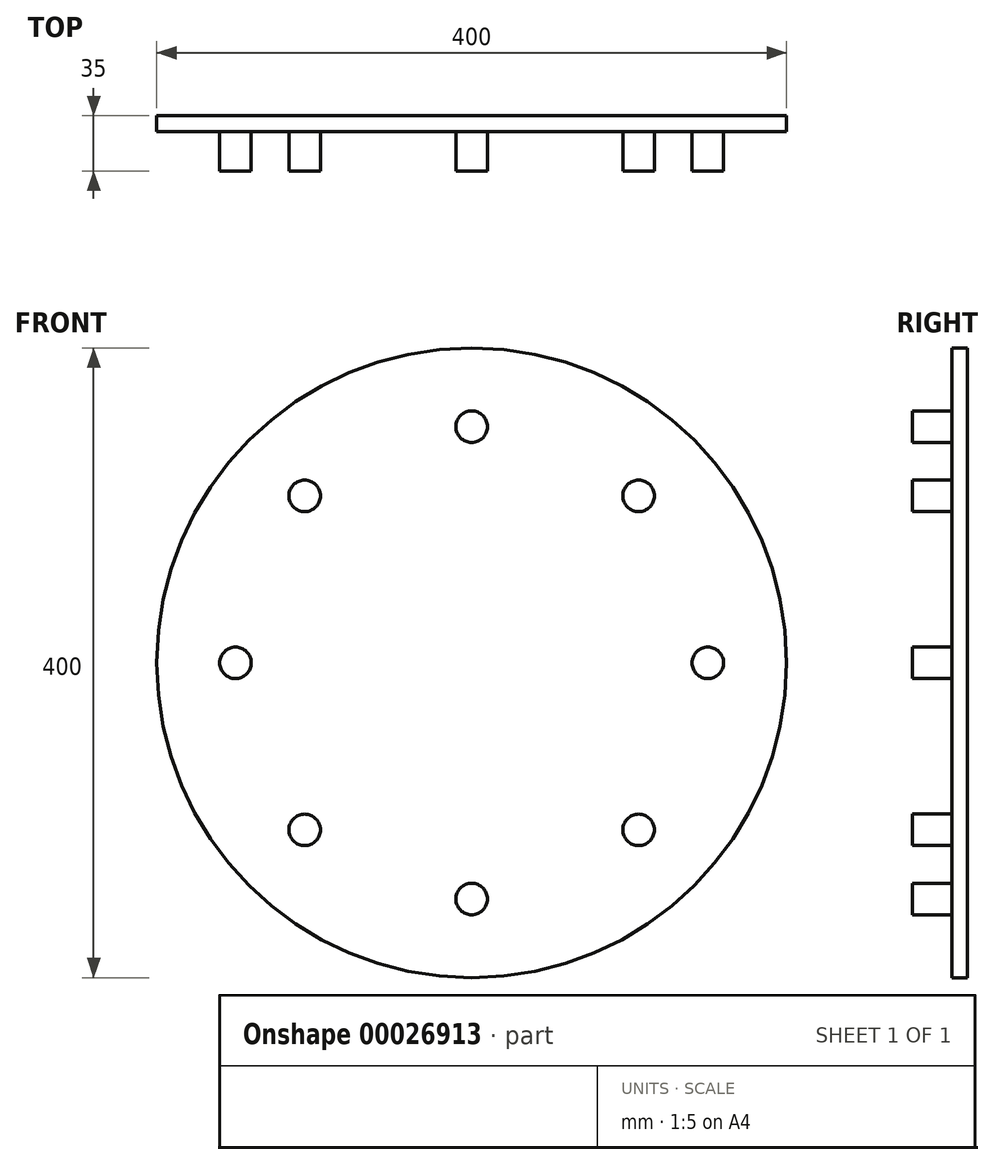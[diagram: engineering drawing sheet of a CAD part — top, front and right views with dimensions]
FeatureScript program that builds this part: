
annotation { "Feature Type Name" : "Feature", "Feature Type Description" : "" }
export const myFeature = defineFeature(function(context is Context, id is Id, definition is map)
    precondition{}
    {
        {
            var Q0;
            Q0=qCreatedBy(makeId("Front.planeOp"),FACE);
            var sketch = newSketch(context, id + "F0", { "sketchPlane" : qUnion([Q0])});
            skCircle(sketch, "E0", {"center": v(0, 0) * mm, "radius": 200 * mm});
            skSolve(sketch);
        }
        {
            var Q0;
            Q0=qSketchRegion(id+"F0",true);
            extrude(context, id + "F1", {"entities" : qUnion([Q0]), "depth" : 10 * mm});
        }
        {
            var Q0;
            Q0=makeQuery(id+"F1.opExtrude","CAP_FACE",FACE,{"disambiguationData":[OSD([sQuery(id+"F0.wireOp",EDGE,"E0")])],"isStart":false});
            var sketch = newSketch(context, id + "F2", { "sketchPlane" : qUnion([Q0])});
            skCircle(sketch, "E1", {"center": v(0, 150) * mm, "radius": 10 * mm});
            skCircle(sketch, "E2.1.0", {"center": v(-106.07, 106.07) * mm, "radius": 10 * mm});
            skCircle(sketch, "E2.2.0", {"center": v(-150, 0) * mm, "radius": 10 * mm});
            skCircle(sketch, "E2.3.0", {"center": v(-106.07, -106.07) * mm, "radius": 10 * mm});
            skCircle(sketch, "E2.4.0", {"center": v(0, -150) * mm, "radius": 10 * mm});
            skCircle(sketch, "E2.5.0", {"center": v(106.07, -106.07) * mm, "radius": 10 * mm});
            skCircle(sketch, "E2.6.0", {"center": v(150, 0) * mm, "radius": 10 * mm});
            skCircle(sketch, "E2.7.0", {"center": v(106.07, 106.07) * mm, "radius": 10 * mm});
            skPoint(sketch, "E2.center", {"position": v(0, 0) * mm});
            skSolve(sketch);
        }
        {
            var Q0;
            Q0=makeQuery(id+"F2.imprint","IMPRINT",FACE,{"disambiguationData":[TD([[makeQuery(id+"F2.imprint","IMPRINT",EDGE,{"derivedFrom":sQuery(id+"F2.wireOp",EDGE,"E2.1.0")}),1.0]])]});
            var Q1;
            Q1=makeQuery(id+"F2.imprint","IMPRINT",FACE,{"disambiguationData":[TD([[makeQuery(id+"F2.imprint","IMPRINT",EDGE,{"derivedFrom":sQuery(id+"F2.wireOp",EDGE,"E1")}),1.0]])]});
            var Q2;
            Q2=makeQuery(id+"F2.imprint","IMPRINT",FACE,{"disambiguationData":[TD([[makeQuery(id+"F2.imprint","IMPRINT",EDGE,{"derivedFrom":sQuery(id+"F2.wireOp",EDGE,"E2.7.0")}),1.0]])]});
            var Q3;
            Q3=makeQuery(id+"F2.imprint","IMPRINT",FACE,{"disambiguationData":[TD([[makeQuery(id+"F2.imprint","IMPRINT",EDGE,{"derivedFrom":sQuery(id+"F2.wireOp",EDGE,"E2.6.0")}),1.0]])]});
            var Q4;
            Q4=makeQuery(id+"F2.imprint","IMPRINT",FACE,{"disambiguationData":[TD([[makeQuery(id+"F2.imprint","IMPRINT",EDGE,{"derivedFrom":sQuery(id+"F2.wireOp",EDGE,"E2.5.0")}),1.0]])]});
            var Q5;
            Q5=makeQuery(id+"F2.imprint","IMPRINT",FACE,{"disambiguationData":[TD([[makeQuery(id+"F2.imprint","IMPRINT",EDGE,{"derivedFrom":sQuery(id+"F2.wireOp",EDGE,"E2.4.0")}),1.0]])]});
            var Q6;
            Q6=makeQuery(id+"F2.imprint","IMPRINT",FACE,{"disambiguationData":[TD([[makeQuery(id+"F2.imprint","IMPRINT",EDGE,{"derivedFrom":sQuery(id+"F2.wireOp",EDGE,"E2.3.0")}),1.0]])]});
            var Q7;
            Q7=makeQuery(id+"F2.imprint","IMPRINT",FACE,{"disambiguationData":[TD([[makeQuery(id+"F2.imprint","IMPRINT",EDGE,{"derivedFrom":sQuery(id+"F2.wireOp",EDGE,"E2.2.0")}),1.0]])]});
            extrude(context, id + "F3", {"entities" : qUnion([Q0, Q1, Q2, Q3, Q4, Q5, Q6, Q7]), "operationType" : NewBodyOperationType.ADD, "depth" : 25 * mm});
        }
    });
